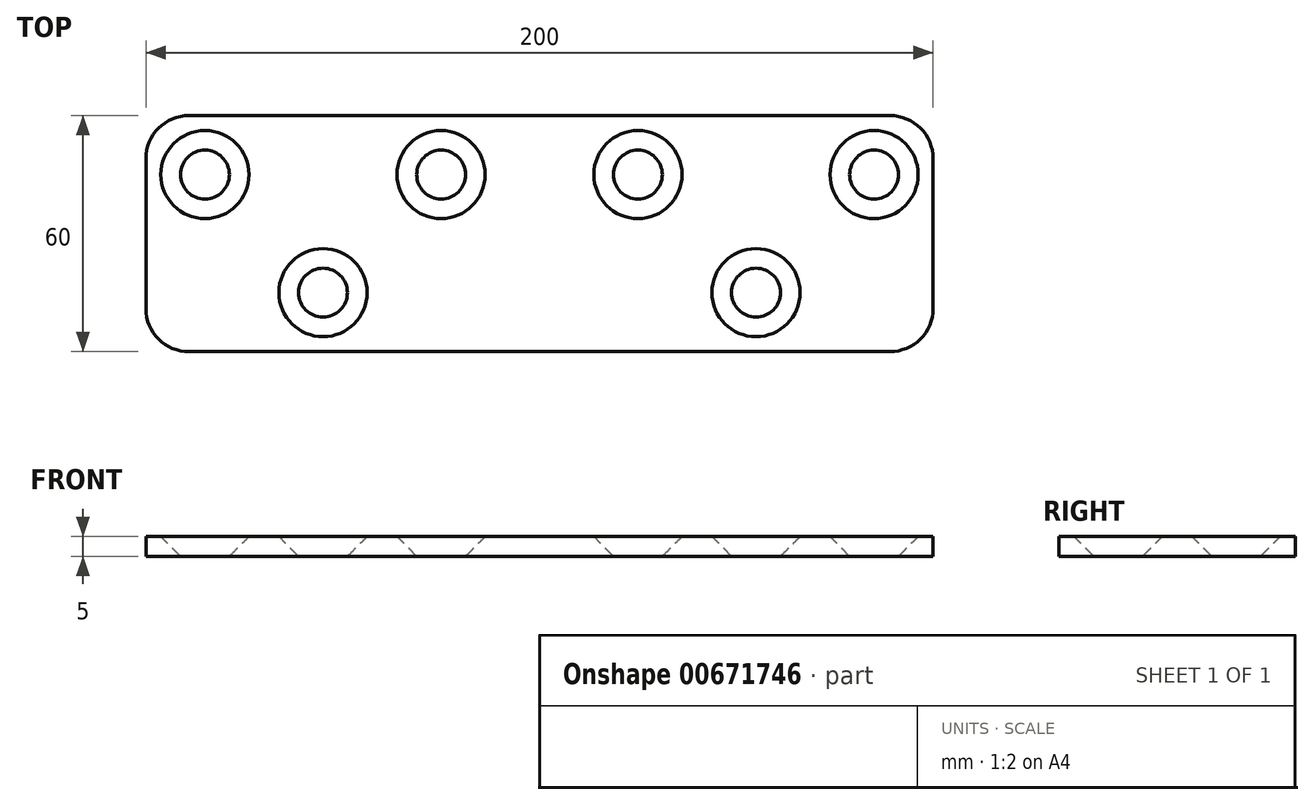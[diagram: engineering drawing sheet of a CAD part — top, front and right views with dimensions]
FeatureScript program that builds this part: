
annotation { "Feature Type Name" : "Feature", "Feature Type Description" : "" }
export const myFeature = defineFeature(function(context is Context, id is Id, definition is map)
    precondition{}
    {
        {
            var Q0;
            Q0=qCreatedBy(makeId("Top.planeOp"),FACE);
            var sketch = newSketch(context, id + "F0", { "sketchPlane" : qUnion([Q0])});
            skLineSegment(sketch, "E0.bottom", {"start": v(100, 30) * mm, "end": v(-100, 30) * mm});
            skLineSegment(sketch, "E0.top", {"start": v(100, -30) * mm, "end": v(-100, -30) * mm});
            skLineSegment(sketch, "E0.left", {"start": v(100, 30) * mm, "end": v(100, -30) * mm});
            skLineSegment(sketch, "E0.right", {"start": v(-100, 30) * mm, "end": v(-100, -30) * mm});
            skPoint(sketch, "E0.middle", {"position": v(0, 0) * mm});
            skSolve(sketch);
        }
        {
            var Q0;
            Q0=makeQuery(id+"F0.imprint","IMPRINT",FACE,{"disambiguationData":[TD([[makeQuery(id+"F0.imprint","IMPRINT",EDGE,{"derivedFrom":sQuery(id+"F0.wireOp",EDGE,"E0.bottom")}),1.0]])]});
            extrude(context, id + "F1", {"entities" : qUnion([Q0]), "depth" : 5 * mm, "offsetDistance" : 25 * mm});
        }
        {
            var Q0;
            Q0=makeQuery(id+"F1.opExtrude","CAP_FACE",FACE,{"disambiguationData":[OSD([sQuery(id+"F0.wireOp",EDGE,"E0.bottom"),sQuery(id+"F0.wireOp",EDGE,"E0.top"),sQuery(id+"F0.wireOp",EDGE,"E0.left"),sQuery(id+"F0.wireOp",EDGE,"E0.right")])],"isStart":false});
            var sketch = newSketch(context, id + "F2", { "sketchPlane" : qUnion([Q0])});
            skCircle(sketch, "E1", {"center": v(-85, 15) * mm, "radius": 5.5 * mm});
            skCircle(sketch, "E2", {"center": v(-25, 15) * mm, "radius": 5.5 * mm});
            skCircle(sketch, "E3", {"center": v(25, 15) * mm, "radius": 5.5 * mm});
            skCircle(sketch, "E4", {"center": v(85, 15) * mm, "radius": 5.5 * mm});
            skCircle(sketch, "E5", {"center": v(55, -15) * mm, "radius": 5.5 * mm});
            skCircle(sketch, "E6", {"center": v(-55, -15) * mm, "radius": 5.5 * mm});
            skSolve(sketch);
        }
        {
            var Q0;
            Q0=sQuery(id+"F2.wireOp",VERTEX,"E1.center");
            var Q1;
            Q1=sQuery(id+"F2.wireOp",VERTEX,"E2.center");
            var Q2;
            Q2=sQuery(id+"F2.wireOp",VERTEX,"E3.center");
            var Q3;
            Q3=sQuery(id+"F2.wireOp",VERTEX,"E6.center");
            var Q4;
            Q4=sQuery(id+"F2.wireOp",VERTEX,"E5.center");
            var Q5;
            Q5=sQuery(id+"F2.wireOp",VERTEX,"E4.center");
            var Q6;
            Q6=makeQuery(id+"F1.opExtrude","SWEPT_BODY",BODY,{"disambiguationData":[OSD([sQuery(id+"F0.wireOp",EDGE,"E0.bottom"),sQuery(id+"F0.wireOp",EDGE,"E0.top"),sQuery(id+"F0.wireOp",EDGE,"E0.left"),sQuery(id+"F0.wireOp",EDGE,"E0.right")])]});
            hole(context, id + "F3", {"style" : HoleStyle.C_SINK, "endStyle" : HoleEndStyle.THROUGH, "standardTappedOrClearance" : lookupTablePath({ "standard" : "ISO", "fit" : "Normal", "size" : "M10", "type" : "Clearance" }), "standardBlindInLast" : lookupTablePath({ "fit" : "Standard", "standard" : "ISO", "size" : "M10", "type" : "Clearance" }), "holeDiameter" : 11 * mm, "cSinkDiameter" : 22.4 * mm, "cSinkAngle" : 90 * degree, "majorDiameter" : 5 * mm, "isTappedThrough" : true, "tappedDepth" : 12 * mm, "tapClearance" : 3, "locations" : qUnion([Q0, Q1, Q2, Q3, Q4, Q5]), "scope" : qUnion([Q6])});
        }
        {
            var Q0;
            Q0=makeQuery(id+"F1.opExtrude","SWEPT_EDGE",EDGE,{"disambiguationData":[OSD([sQuery(id+"F0.wireOp",EDGE,"E0.bottom"),sQuery(id+"F0.wireOp",EDGE,"E0.right")])]});
            var Q1;
            Q1=makeQuery(id+"F1.opExtrude","SWEPT_EDGE",EDGE,{"disambiguationData":[OSD([sQuery(id+"F0.wireOp",EDGE,"E0.top"),sQuery(id+"F0.wireOp",EDGE,"E0.right")])]});
            var Q2;
            Q2=makeQuery(id+"F1.opExtrude","SWEPT_EDGE",EDGE,{"disambiguationData":[OSD([sQuery(id+"F0.wireOp",EDGE,"E0.top"),sQuery(id+"F0.wireOp",EDGE,"E0.left")])]});
            var Q3;
            Q3=makeQuery(id+"F1.opExtrude","SWEPT_EDGE",EDGE,{"disambiguationData":[OSD([sQuery(id+"F0.wireOp",EDGE,"E0.bottom"),sQuery(id+"F0.wireOp",EDGE,"E0.left")])]});
            fillet(context, id + "F4", {"entities" : qUnion([Q0, Q1, Q2, Q3]), "radius" : 11 * mm, "tangentPropagation" : true, "allowEdgeOverflow" : false});
        }
    });
